# Revit family: Hager-Volta-IP30-Hollow_wall-leer-CH-de
name_source: partatom
category: Electrical Equipment
units: mm (PartAtom-declared; Revit-internal decimal feet)

## family parameters
Cut with Voids When Loaded = No
Host = Face
Panel Configuration = Two Columns, Circuits Across
Part Type = Panelboard
Room Calculation Point = No
Round Connector Dimension = Use Diameter
Shared = No

## types (5) — shared parameters
EF000003 - Montageart = EV000128 - Hohlwand
EF000007 - Farbe = EV000202 - weiß
EF000008 - Breite = 330 mm
EF000049 - Tiefe = 94 mm  [stored 0.308399 ft]
EF000116 - RAL-Nummer = 9010
EF000118 - Mit Montageplatte = No
EF000218 - Einbautiefe = 90 mm  [stored 0.295276 ft]
EF000846 - Einbaubreite = 314 mm  [stored 1.03018 ft]
EF001062 - EMV-Ausführung = Yes
EF001088 - Anbaumöglichkeit = Yes
EF001131 - Innentiefe = 92 mm
EF001134 - DIN-Schiene = No
EF001596 - Werkstoff des Gehäuses = EV000139 - Kunststoff
EF002950 - Breite in Teilungseinheiten = 12
EF006244 - Transparenter Deckel/Tür = No
EF006306 - Mit Schloss = No
EF009212 - Ausführung Deckel = EV000116 - geschlossen
EF015776 - Erdungsklemmenblock = No
EF015777 - Neutralleiterklemmenblock = No
EF015941 - Signaldurchlassende Tür = No
HG000002 - Mit tür = No
HG000003 - Bereich = Volta
HG000005 - Dicke = 3 mm  [stored 0.00984252 ft]
HG000006 - Unterputz = Yes
HG000009 - Doppelflügeligen Tür = No
HG000010 - Asymmetrische Türen = No
HG000011 - Leere Reihen von unten = No
HG000017 - Distanz zwischen den Polen = 18 mm  [stored 0.0590551 ft]
Manufacturer = Hager
Type Comments = Volta
zero-valued in all types: Default Elevation, HG000001 - Anzahl der Spalten, HG000007 - Anzahl der leeren Spalten, HG000008 - Anzahl der leeren Reihen

## per-type parameters (varying)
| type | EF000040 - Höhe | EF000266 - Anzahl der Reihen | EF000332 - Einbauhöhe | HG000004 - Herstellerreferenz | Model |
| Unterputz  B330 H355 T94.5 12 Teilungseinheiten - VH12NK | 355 mm | 1 | 346 mm | VH12NK | VH12NK |
| Unterputz  B330 H484 T94.5 12 Teilungseinheiten - VH24NK | 484 mm | 2 | 471 mm | VH24NK | VH24NK |
| Unterputz  B330 H609 T94.5 12 Teilungseinheiten - VH36NK | 609 mm | 3 | 596 mm | VH36NK | VH36NK |
| Unterputz  B330 H734 T94.5 12 Teilungseinheiten - VH48NK | 734 mm | 4 | 721 mm | VH48NK | VH48NK |
| Unterputz  B330 H880 T94.5 12 Teilungseinheiten - VH60NK | 880 mm  [stored 2.88714 ft] | 5 | 846 mm  [stored 2.77559 ft] | VH60NK | VH60NK |

note: [stored X ft] marks values corroborated as IEEE doubles in the binary element streams (Revit-internal decimal feet)

## geometry (parser evidence)
native form markers: Sweep x17
no freeform markers — native parametric forms only
